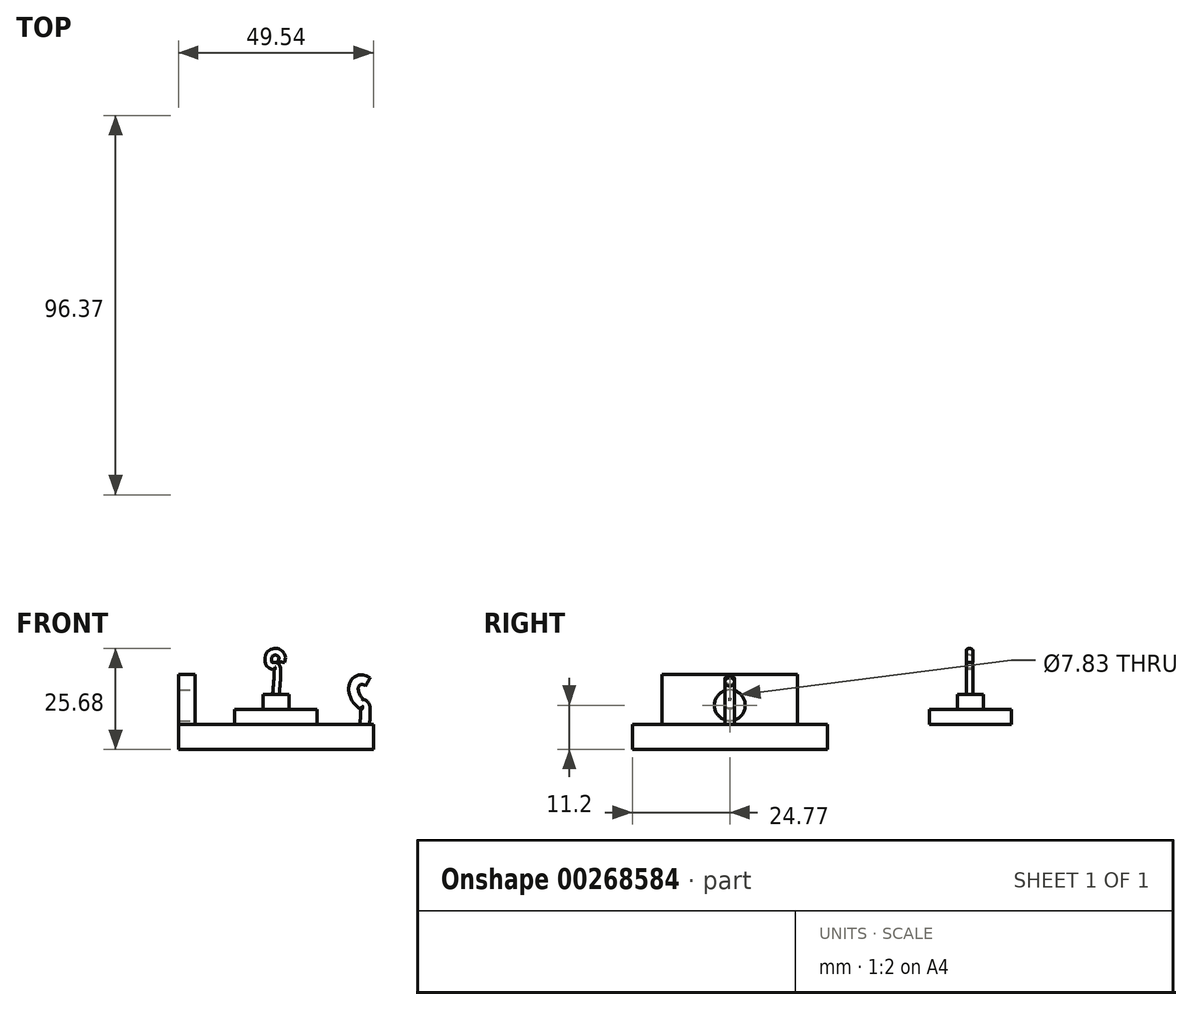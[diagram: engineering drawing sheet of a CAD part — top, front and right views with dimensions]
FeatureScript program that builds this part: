
annotation { "Feature Type Name" : "Feature", "Feature Type Description" : "" }
export const myFeature = defineFeature(function(context is Context, id is Id, definition is map)
    precondition{}
    {
        {
            var Q0;
            Q0=qCreatedBy(makeId("Top.planeOp"),FACE);
            var sketch = newSketch(context, id + "F0", { "sketchPlane" : qUnion([Q0])});
            skLineSegment(sketch, "E0.bottom", {"start": v(-24.77, 24.77) * mm, "end": v(24.77, 24.77) * mm});
            skLineSegment(sketch, "E0.top", {"start": v(-24.77, -24.77) * mm, "end": v(24.77, -24.77) * mm});
            skLineSegment(sketch, "E0.left", {"start": v(-24.77, 24.77) * mm, "end": v(-24.77, -24.77) * mm});
            skLineSegment(sketch, "E0.right", {"start": v(24.77, 24.77) * mm, "end": v(24.77, -24.77) * mm});
            skPoint(sketch, "E0.middle", {"position": v(0, 0) * mm});
            skSolve(sketch);
        }
        {
            var Q0;
            Q0=makeQuery(id+"F0.imprint","IMPRINT",FACE,{"disambiguationData":[TD([[makeQuery(id+"F0.imprint","IMPRINT",EDGE,{"derivedFrom":sQuery(id+"F0.wireOp",EDGE,"E0.bottom")}),-1.0]])]});
            extrude(context, id + "F1", {"entities" : qUnion([Q0]), "oppositeDirection" : true, "depth" : 6.35 * mm});
        }
        {
            var Q0;
            Q0=qCreatedBy(makeId("Top.planeOp"),FACE);
            var sketch = newSketch(context, id + "F2", { "sketchPlane" : qUnion([Q0])});
            skCircle(sketch, "E1", {"center": v(22.56, 0) * mm, "radius": 1.22 * mm});
            skSolve(sketch);
        }
        {
            var Q0;
            Q0=qCreatedBy(makeId("Front.planeOp"),FACE);
            var sketch = newSketch(context, id + "F3", { "sketchPlane" : qUnion([Q0])});
            skFitSpline(sketch, "E2", {"points": [v(22.56, 0) * mm, v(21.72, 5.21) * mm, v(20.38, 6.72) * mm, v(19.7, 9.3) * mm, v(20.65, 11.06) * mm, v(23.34, 10.8) * mm], "startDerivative": vector(4.9, 62.63) * mm, "endDerivative": vector(18.62, -12.27) * mm});
            skSolve(sketch);
        }
        {
            var Q0;
            Q0=makeQuery(id+"F2.imprint","IMPRINT",FACE,{"disambiguationData":[TD([[makeQuery(id+"F2.imprint","IMPRINT",EDGE,{"derivedFrom":sQuery(id+"F2.wireOp",EDGE,"E1")}),1.0]])]});
            var Q1;
            Q1=sQuery(id+"F3.wireOp",EDGE,"E2");
            sweep(context, id + "F4", {"profiles" : qUnion([Q0]), "path" : qUnion([Q1])});
        }
        {
            var Q0;
            Q0=qCreatedBy(makeId("Top.planeOp"),FACE);
            var sketch = newSketch(context, id + "F5", { "sketchPlane" : qUnion([Q0])});
            skLineSegment(sketch, "E3.bottom", {"start": v(-20.52, -17.25) * mm, "end": v(-24.77, -17.25) * mm});
            skLineSegment(sketch, "E3.top", {"start": v(-20.52, 17.25) * mm, "end": v(-24.77, 17.25) * mm});
            skLineSegment(sketch, "E3.left", {"start": v(-20.52, -17.25) * mm, "end": v(-20.52, 17.25) * mm});
            skLineSegment(sketch, "E3.right", {"start": v(-24.77, -17.25) * mm, "end": v(-24.77, 17.25) * mm});
            skPoint(sketch, "E3.middle", {"position": v(-22.65, 0) * mm});
            skSolve(sketch);
        }
        {
            var Q0;
            Q0=makeQuery(id+"F5.imprint","IMPRINT",FACE,{"disambiguationData":[TD([[makeQuery(id+"F5.imprint","IMPRINT",EDGE,{"derivedFrom":sQuery(id+"F5.wireOp",EDGE,"E3.bottom")}),-1.0]])]});
            extrude(context, id + "F6", {"entities" : qUnion([Q0]), "operationType" : NewBodyOperationType.ADD, "depth" : 12.7 * mm});
        }
        {
            var Q0;
            Q0=makeQuery(id+"F6.opExtrude","SWEPT_FACE",FACE,{"disambiguationData":[OSD([sQuery(id+"F5.wireOp",EDGE,"E3.left")])]});
            var sketch = newSketch(context, id + "F7", { "sketchPlane" : qUnion([Q0])});
            skCircle(sketch, "E4", {"center": v(0, 4.85) * mm, "radius": 3.91 * mm});
            skSolve(sketch);
        }
        {
            var Q0;
            Q0=makeQuery(id+"F7.imprint","IMPRINT",FACE,{"disambiguationData":[TD([[makeQuery(id+"F7.imprint","IMPRINT",EDGE,{"derivedFrom":sQuery(id+"F7.wireOp",EDGE,"E4")}),1.0]])]});
            var Q1;
            Q1=sQuery(id+"F7.wireOp",EDGE,"E4");
            extrude(context, id + "F8", {"entities" : qUnion([Q0]), "operationType" : NewBodyOperationType.REMOVE, "surfaceEntities" : qUnion([Q1]), "oppositeDirection" : true, "depth" : 25.4 * mm});
        }
        {
            var Q0;
            Q0=qCreatedBy(makeId("Top.planeOp"),FACE);
            var sketch = newSketch(context, id + "F9", { "sketchPlane" : qUnion([Q0])});
            skCircle(sketch, "E5", {"center": v(0, 61.15) * mm, "radius": 10.45 * mm});
            skSolve(sketch);
        }
        {
            var Q0;
            Q0=makeQuery(id+"F9.imprint","IMPRINT",FACE,{"disambiguationData":[TD([[makeQuery(id+"F9.imprint","IMPRINT",EDGE,{"derivedFrom":sQuery(id+"F9.wireOp",EDGE,"E5")}),1.0]])]});
            extrude(context, id + "F10", {"entities" : qUnion([Q0]), "depth" : 3.8 * mm});
        }
        {
            var Q0;
            Q0=makeQuery(id+"F10.opExtrude","CAP_FACE",FACE,{"disambiguationData":[OSD([sQuery(id+"F9.wireOp",EDGE,"E5")])],"isStart":false});
            var sketch = newSketch(context, id + "F11", { "sketchPlane" : qUnion([Q0])});
            skCircle(sketch, "E6", {"center": v(0, 61.15) * mm, "radius": 3.27 * mm});
            skSolve(sketch);
        }
        {
            var Q0;
            Q0=makeQuery(id+"F11.imprint","IMPRINT",FACE,{"disambiguationData":[TD([[makeQuery(id+"F11.imprint","IMPRINT",EDGE,{"derivedFrom":sQuery(id+"F11.wireOp",EDGE,"E6")}),1.0]])]});
            var Q1;
            Q1=sQuery(id+"F11.wireOp",EDGE,"E6");
            extrude(context, id + "F12", {"entities" : qUnion([Q0]), "surfaceEntities" : qUnion([Q1]), "depth" : 3.8 * mm});
        }
        {
            var Q0;
            Q0=qCreatedBy(makeId("Front.planeOp"),FACE);
            cPlane(context, id + "F13", {"entities" : qUnion([Q0]), "cplaneType" : CPlaneType.OFFSET, "offset" : 60.96 * mm, "oppositeDirection" : true, "width" : 152.4 * mm, "height" : 152.4 * mm});
        }
        {
            var Q0;
            Q0=qCreatedBy(id+"F13.planeOp",FACE);
            var sketch = newSketch(context, id + "F14", { "sketchPlane" : qUnion([Q0])});
            skFitSpline(sketch, "E7", {"points": [v(0, 7.62) * mm, v(0, 14.87) * mm, v(-0.95, 14.87) * mm, v(-1.85, 15.7) * mm, v(-1.63, 17.72) * mm, v(0, 18.48) * mm, v(1.21, 17.83) * mm, v(1.38, 15.86) * mm], "startDerivative": vector(3.47, 42.44) * mm, "endDerivative": vector(-7.56, -26.78) * mm});
            skSolve(sketch);
        }
        {
            var Q0;
            Q0=makeQuery(id+"F12.opExtrude","CAP_FACE",FACE,{"disambiguationData":[OSD([sQuery(id+"F11.wireOp",EDGE,"E6")])],"isStart":false});
            var sketch = newSketch(context, id + "F15", { "sketchPlane" : qUnion([Q0])});
            skCircle(sketch, "E8", {"center": v(0, 60.96) * mm, "radius": 0.85 * mm});
            skSolve(sketch);
        }
        {
            var Q0;
            Q0=makeQuery(id+"F15.imprint","IMPRINT",FACE,{"disambiguationData":[TD([[makeQuery(id+"F15.imprint","IMPRINT",EDGE,{"derivedFrom":sQuery(id+"F15.wireOp",EDGE,"E8")}),1.0]])]});
            var Q1;
            Q1=sQuery(id+"F14.wireOp",EDGE,"E7");
            sweep(context, id + "F16", {"operationType" : NewBodyOperationType.ADD, "profiles" : qUnion([Q0]), "path" : qUnion([Q1])});
        }
    });
